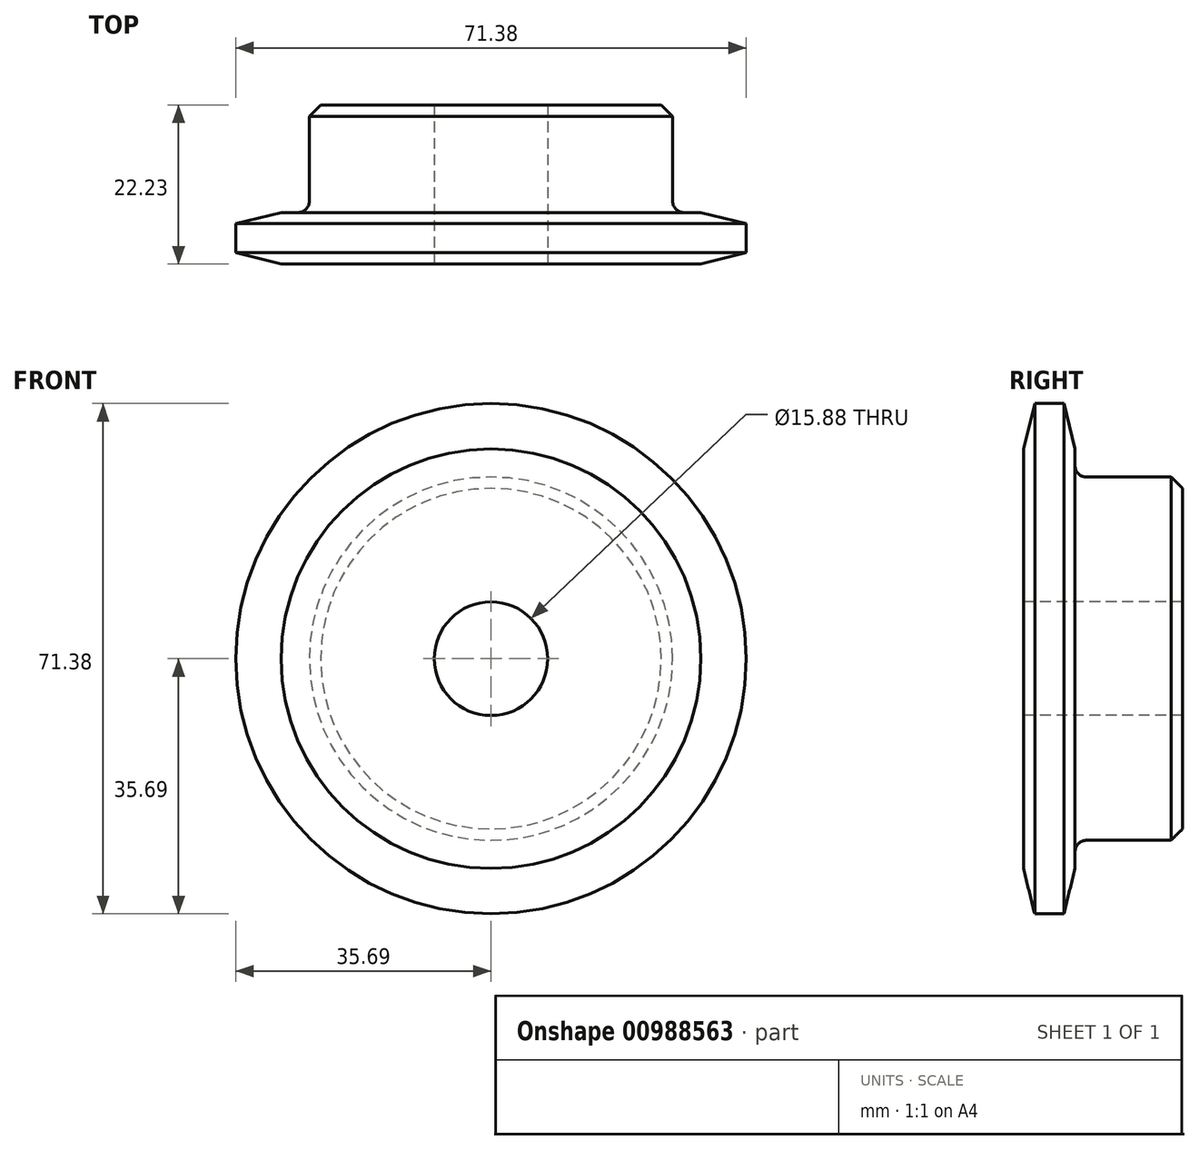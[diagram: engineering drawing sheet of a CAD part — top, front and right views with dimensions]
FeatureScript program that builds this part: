
annotation { "Feature Type Name" : "Feature", "Feature Type Description" : "" }
export const myFeature = defineFeature(function(context is Context, id is Id, definition is map)
    precondition{}
    {
        {
            var Q0;
            Q0=qCreatedBy(makeId("Right.planeOp"),FACE);
            var sketch = newSketch(context, id + "F0", { "sketchPlane" : qUnion([Q0])});
            skLineSegment(sketch, "E0", {"start": v(0, 0) * mm, "end": v(22.23, 0) * mm, "construction": true});
            skLineSegment(sketch, "E1.bottom", {"start": v(0, 7.94) * mm, "end": v(7.21, 7.94) * mm});
            skLineSegment(sketch, "E1.top", {"start": v(0, 35.69) * mm, "end": v(7.21, 35.69) * mm});
            skLineSegment(sketch, "E1.left", {"start": v(0, 7.94) * mm, "end": v(0, 35.69) * mm});
            skLineSegment(sketch, "E1.right", {"start": v(7.21, 7.94) * mm, "end": v(7.21, 35.69) * mm});
            skLineSegment(sketch, "E2.bottom", {"start": v(0, 7.94) * mm, "end": v(22.23, 7.94) * mm});
            skLineSegment(sketch, "E2.top", {"start": v(0, 25.4) * mm, "end": v(22.23, 25.4) * mm});
            skLineSegment(sketch, "E2.left", {"start": v(0, 7.94) * mm, "end": v(0, 25.4) * mm});
            skLineSegment(sketch, "E2.right", {"start": v(22.23, 7.94) * mm, "end": v(22.23, 25.4) * mm});
            skLineSegment(sketch, "E3.MirrorCS", {"start": v(0, -7.94) * mm, "end": v(7.21, -7.94) * mm});
            skLineSegment(sketch, "E4.MirrorCS", {"start": v(0, -35.69) * mm, "end": v(7.21, -35.69) * mm});
            skLineSegment(sketch, "E5.MirrorCS", {"start": v(0, -7.94) * mm, "end": v(0, -25.4) * mm});
            skLineSegment(sketch, "E6.MirrorCS", {"start": v(0, -7.94) * mm, "end": v(0, -35.69) * mm});
            skLineSegment(sketch, "E7.MirrorCS", {"start": v(0, -25.4) * mm, "end": v(22.23, -25.4) * mm});
            skLineSegment(sketch, "E8.MirrorCS", {"start": v(22.23, -7.94) * mm, "end": v(22.23, -25.4) * mm});
            skLineSegment(sketch, "E9.MirrorCS", {"start": v(0, -7.94) * mm, "end": v(22.23, -7.94) * mm});
            skLineSegment(sketch, "E10.MirrorCS", {"start": v(7.21, -7.94) * mm, "end": v(7.21, -35.69) * mm});
            skSolve(sketch);
        }
        {
            var Q0;
            {var subQ0=sQuery(id+"F0.wireOp",EDGE,"E1.top");Q0=makeQuery(id+"F0.imprint","IMPRINT",FACE,{"disambiguationData":[TD([[makeQuery(id+"F0.imprint","IMPRINT",EDGE,{"derivedFrom":subQ0}),-1.0]])]});}
            var Q1;
            {var subQ0=sQuery(id+"F0.wireOp",EDGE,"E1.bottom");Q1=makeQuery(id+"F0.imprint","IMPRINT",FACE,{"disambiguationData":[TD([[makeQuery(id+"F0.imprint","IMPRINT",EDGE,{"derivedFrom":subQ0}),1.0]])]});}
            var Q2;
            {var subQ0=sQuery(id+"F0.wireOp",EDGE,"E2.bottom");Q2=makeQuery(id+"F0.imprint","IMPRINT",FACE,{"disambiguationData":[TD([[makeQuery(id+"F0.imprint","IMPRINT",EDGE,{"derivedFrom":subQ0}),1.0]])]});}
            var Q3;
            Q3=sQuery(id+"F0.wireOp",EDGE,"E0");
            revolve(context, id + "F1", {"surfaceOperationType" : NewSurfaceOperationType.NEW, "entities" : qUnion([Q0, Q1, Q2]), "axis" : qUnion([Q3]), "revolveType" : RevolveType.FULL});
        }
        {
            var Q0;
            Q0=makeQuery(id+"F1.opRevolve","SWEPT_EDGE",EDGE,{"disambiguationData":[OSD([sQuery(id+"F0.wireOp",EDGE,"E1.right"),sQuery(id+"F0.wireOp",EDGE,"E2.top")])]});
            fillet(context, id + "F2", {"entities" : qUnion([Q0]), "radius" : 1.59 * mm, "tangentPropagation" : true, "allowEdgeOverflow" : false});
        }
        {
            var Q0;
            Q0=makeQuery(id+"F1.opRevolve","SWEPT_EDGE",EDGE,{"disambiguationData":[OSD([sQuery(id+"F0.wireOp",EDGE,"E2.top"),sQuery(id+"F0.wireOp",EDGE,"E2.right")])]});
            chamfer(context, id + "F3", {"entities" : qUnion([Q0]), "width" : 1.59 * mm, "tangentPropagation" : true});
        }
        {
            var Q0;
            Q0=makeQuery(id+"F1.opRevolve","SWEPT_EDGE",EDGE,{"disambiguationData":[OSD([sQuery(id+"F0.wireOp",EDGE,"E1.top"),sQuery(id+"F0.wireOp",EDGE,"E1.right")])]});
            var Q1;
            Q1=makeQuery(id+"F1.opRevolve","SWEPT_EDGE",EDGE,{"disambiguationData":[OSD([sQuery(id+"F0.wireOp",EDGE,"E1.top"),sQuery(id+"F0.wireOp",EDGE,"E1.left")])]});
            chamfer(context, id + "F4", {"entities" : qUnion([Q0, Q1]), "chamferType" : ChamferType.TWO_OFFSETS, "width1" : 6.35 * mm, "oppositeDirection" : true, "width2" : 1.57 * mm, "tangentPropagation" : true});
        }
    });
